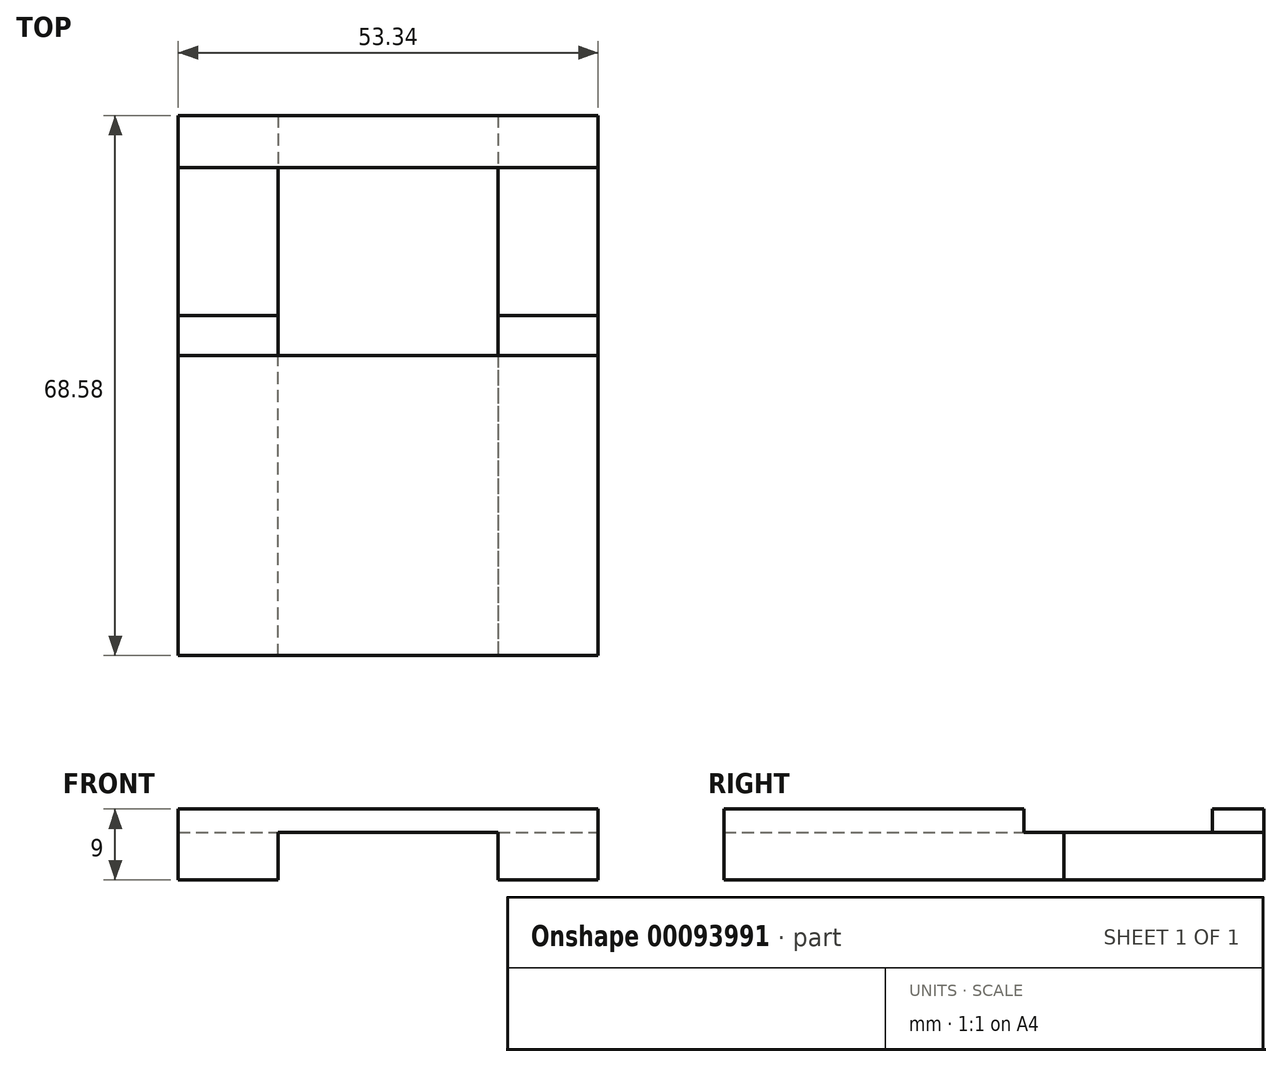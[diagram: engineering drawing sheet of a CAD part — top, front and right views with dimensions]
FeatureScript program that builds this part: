
annotation { "Feature Type Name" : "Feature", "Feature Type Description" : "" }
export const myFeature = defineFeature(function(context is Context, id is Id, definition is map)
    precondition{}
    {
        {
            var Q0;
            Q0=qCreatedBy(makeId("Top.planeOp"),FACE);
            var sketch = newSketch(context, id + "F0", { "sketchPlane" : qUnion([Q0])});
            skLineSegment(sketch, "E0.bottom", {"start": v(0, 0) * mm, "end": v(12.7, 0) * mm});
            skLineSegment(sketch, "E0.top", {"start": v(0, 43.18) * mm, "end": v(12.7, 43.18) * mm});
            skLineSegment(sketch, "E0.left", {"start": v(0, 0) * mm, "end": v(0, 43.18) * mm});
            skLineSegment(sketch, "E0.right", {"start": v(12.7, 0) * mm, "end": v(12.7, 43.18) * mm});
            skLineSegment(sketch, "E1.bottom", {"start": v(40.64, 43.18) * mm, "end": v(53.34, 43.18) * mm});
            skLineSegment(sketch, "E1.top", {"start": v(40.64, 0) * mm, "end": v(53.34, 0) * mm});
            skLineSegment(sketch, "E1.left", {"start": v(40.64, 43.18) * mm, "end": v(40.64, 0) * mm});
            skLineSegment(sketch, "E1.right", {"start": v(53.34, 43.18) * mm, "end": v(53.34, 0) * mm});
            skSolve(sketch);
        }
        {
            var Q0;
            Q0=makeQuery(id+"F0.imprint","IMPRINT",FACE,{"disambiguationData":[TD([[makeQuery(id+"F0.imprint","IMPRINT",EDGE,{"derivedFrom":sQuery(id+"F0.wireOp",EDGE,"E0.bottom")}),1.0]])]});
            var Q1;
            Q1=makeQuery(id+"F0.imprint","IMPRINT",FACE,{"disambiguationData":[TD([[makeQuery(id+"F0.imprint","IMPRINT",EDGE,{"derivedFrom":sQuery(id+"F0.wireOp",EDGE,"E1.bottom")}),-1.0]])]});
            extrude(context, id + "F1", {"entities" : qUnion([Q0, Q1]), "depth" : 6 * mm});
        }
        {
            var Q0;
            Q0=makeQuery(id+"F1.opExtrude","SWEPT_FACE",FACE,{"disambiguationData":[OSD([sQuery(id+"F0.wireOp",EDGE,"E0.top")])]});
            var Q1;
            Q1=makeQuery(id+"F1.opExtrude","SWEPT_FACE",FACE,{"disambiguationData":[OSD([sQuery(id+"F0.wireOp",EDGE,"E1.bottom")])]});
            extrude(context, id + "F2", {"entities" : qUnion([Q0, Q1]), "depth" : 25.4 * mm});
        }
        {
            var Q0;
            {var subQ0=sQuery(id+"F0.wireOp",EDGE,"E0.top");Q0=makeQuery(id+"F2.opExtrude","SWEPT_FACE",FACE,{"disambiguationData":[OSD([subQ0]),TDD([makeQuery(id+"F1.opExtrude","CAP_EDGE",EDGE,{"disambiguationData":[OSD([subQ0])],"isStart":false})])]});}
            var sketch = newSketch(context, id + "F3", { "sketchPlane" : qUnion([Q0])});
            skLineSegment(sketch, "E2.bottom", {"start": v(0, 62.02) * mm, "end": v(53.34, 62.02) * mm});
            skLineSegment(sketch, "E2.top", {"start": v(0, 68.58) * mm, "end": v(53.34, 68.58) * mm});
            skLineSegment(sketch, "E2.left", {"start": v(0, 62.02) * mm, "end": v(0, 68.58) * mm});
            skLineSegment(sketch, "E2.right", {"start": v(53.34, 62.02) * mm, "end": v(53.34, 68.58) * mm});
            skSolve(sketch);
        }
        {
            var Q0;
            {var subQ0=sQuery(id+"F3.wireOp",EDGE,"E2.right");Q0=makeQuery(id+"F3.imprint","IMPRINT",FACE,{"disambiguationData":[TD([[makeQuery(id+"F3.imprint","IMPRINT",EDGE,{"derivedFrom":subQ0}),1.0]])]});}
            var Q1;
            {var subQ0=sQuery(id+"F3.wireOp",EDGE,"E2.left");Q1=makeQuery(id+"F3.imprint","IMPRINT",FACE,{"disambiguationData":[TD([[makeQuery(id+"F3.imprint","IMPRINT",EDGE,{"derivedFrom":subQ0}),1.0]])]});}
            extrude(context, id + "F4", {"entities" : qUnion([Q0, Q1]), "depth" : 3 * mm});
        }
        {
            var Q0;
            Q0=makeQuery(id+"F1.opExtrude","CAP_FACE",FACE,{"disambiguationData":[OSD([sQuery(id+"F0.wireOp",EDGE,"E0.bottom"),sQuery(id+"F0.wireOp",EDGE,"E0.top"),sQuery(id+"F0.wireOp",EDGE,"E0.left"),sQuery(id+"F0.wireOp",EDGE,"E0.right")])],"isStart":false});
            var sketch = newSketch(context, id + "F5", { "sketchPlane" : qUnion([Q0])});
            skLineSegment(sketch, "E3.bottom", {"start": v(0, 0) * mm, "end": v(53.34, 0) * mm});
            skLineSegment(sketch, "E3.top", {"start": v(0, 38.1) * mm, "end": v(53.34, 38.1) * mm});
            skLineSegment(sketch, "E3.left", {"start": v(0, 0) * mm, "end": v(0, 38.1) * mm});
            skLineSegment(sketch, "E3.right", {"start": v(53.34, 0) * mm, "end": v(53.34, 38.1) * mm});
            skSolve(sketch);
        }
        {
            var Q0;
            {var subQ3=sQuery(id+"F5.wireOp",EDGE,"E3.right");Q0=makeQuery(id+"F5.imprint","IMPRINT",FACE,{"disambiguationData":[TD([[makeQuery(id+"F5.imprint","IMPRINT",EDGE,{"derivedFrom":subQ3}),1.0]])]});}
            var Q1;
            {var subQ0=sQuery(id+"F5.wireOp",EDGE,"E3.left");Q1=makeQuery(id+"F5.imprint","IMPRINT",FACE,{"disambiguationData":[TD([[makeQuery(id+"F5.imprint","IMPRINT",EDGE,{"derivedFrom":subQ0}),-1.0]])]});}
            extrude(context, id + "F6", {"entities" : qUnion([Q0, Q1]), "operationType" : NewBodyOperationType.ADD, "depth" : 3 * mm});
        }
    });
